# Revit family: QF_BOURGEAT_Conteneurs_Isothermes_Modèles_multi_standards_à_ouverture_Frontale
name_source: partatom
category: Equipement spécialisé
revit_build: Autodesk Revit 2015 (Build: 20140606_1530(x64)
units: mm (PartAtom-declared; Revit-internal decimal feet)

## types (2) — shared parameters
Certification = NF Hygiene alimentaire
Charge max = 90.00 kg
Fabricant = BOURGEAT
Longueur hors tout = 592 mm  [stored 1.94226 ft]
Nature isolant = Mousse sans PU
Profondeur hors tout = 767 mm  [stored 2.5164 ft]
Spécification du Fabricant = Conteneur isotherme
URL catalogue = http://www.bourgeat.fr

## per-type parameters (varying)
| type | Capacité en bacs inox | Capacité en bacs polycarbonate | Capacité en plaques 600x400 | Conteneur haut | Hauteur hors tout | Modèle | Poids net à vide |
| 1 module avec roulettes | 9 GN1/1 H65 mm ou 6 GN1/1 H100 mm | 8 GN1/1 H65 mm ou 5 GN1/1 H100 mm + 1GN1/1 H 65 mm | 12 ou 9 | Non | 1032 mm  [stored 3.38583 ft] | 822301 | 43.00 kg |
| 2 modules avec roulettes | 2x9 GN1/1 H65 mm ou 2x6 GN1/1 H100 mm | 2x8 GN1/1 H65 mm ou 2x5 GN1/1 H100 mm + 2x1GN1/1 H 65 mm | 2x12 ou 2x9 | Oui | 1892 mm  [stored 6.20735 ft] | 823105 | 82.00 kg |

note: [stored X ft] marks values corroborated as IEEE doubles in the binary element streams (Revit-internal decimal feet)
